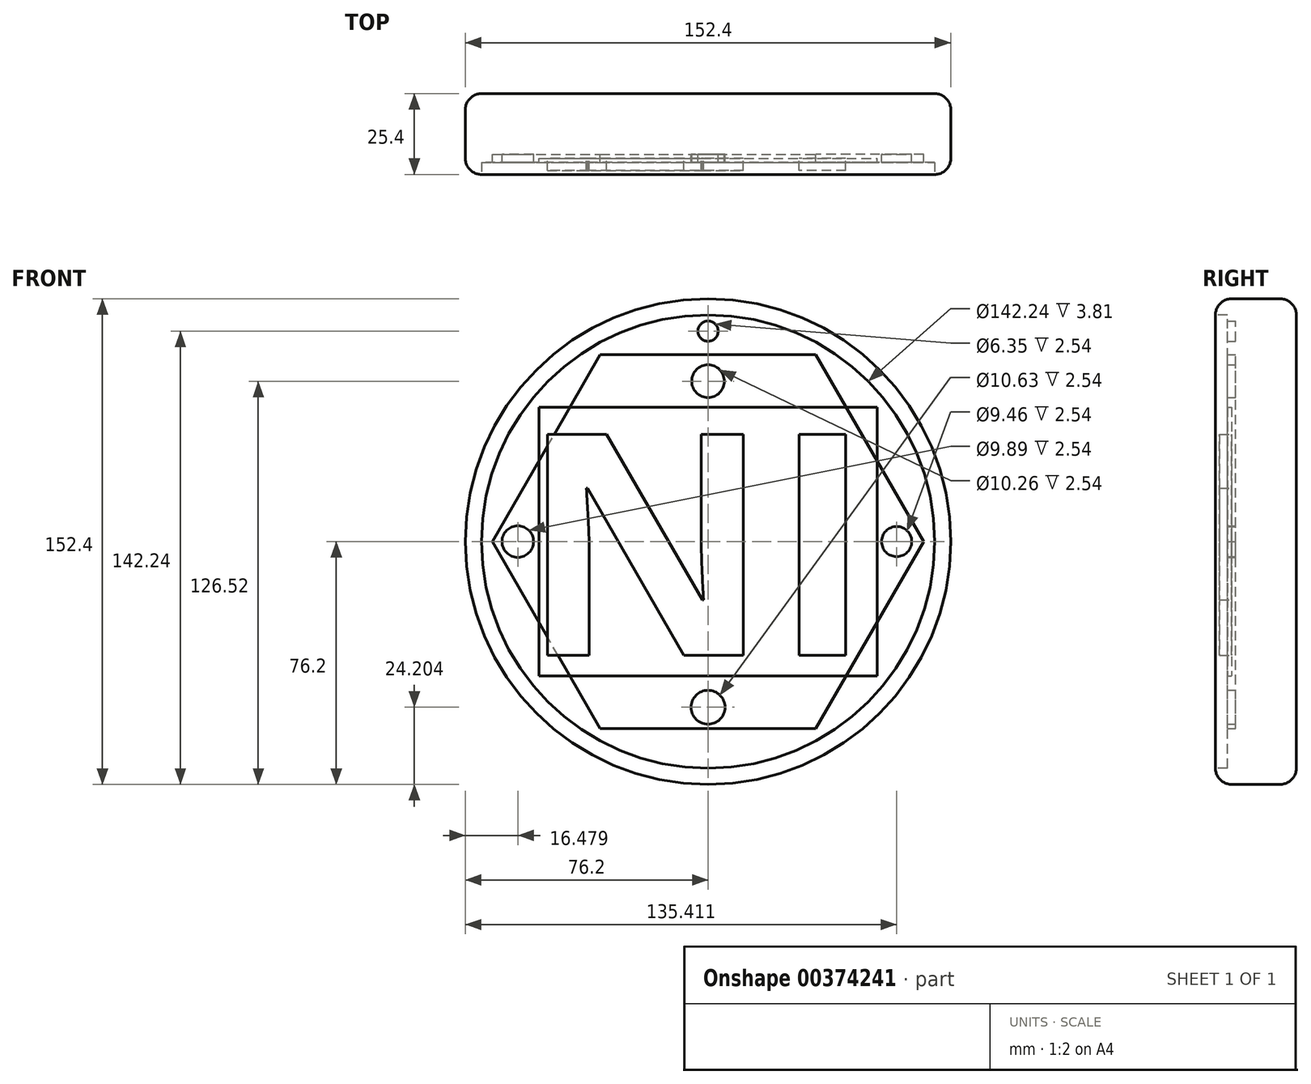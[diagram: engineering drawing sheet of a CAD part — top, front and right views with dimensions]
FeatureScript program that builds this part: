
annotation { "Feature Type Name" : "Feature", "Feature Type Description" : "" }
export const myFeature = defineFeature(function(context is Context, id is Id, definition is map)
    precondition{}
    {
        {
            var Q0;
            Q0=qCreatedBy(makeId("Front.planeOp"),FACE);
            var sketch = newSketch(context, id + "F0", { "sketchPlane" : qUnion([Q0])});
            skCircle(sketch, "E0", {"center": v(0, 0) * mm, "radius": 76.2 * mm});
            skSolve(sketch);
        }
        {
            var Q0;
            Q0=makeQuery(id+"F0.imprint","IMPRINT",FACE,{"disambiguationData":[TD([[makeQuery(id+"F0.imprint","IMPRINT",EDGE,{"derivedFrom":sQuery(id+"F0.wireOp",EDGE,"E0")}),1.0]])]});
            extrude(context, id + "F1", {"entities" : qUnion([Q0]), "depth" : 25.4 * mm});
        }
        {
            var Q0;
            Q0=makeQuery(id+"F1.opExtrude","CAP_EDGE",EDGE,{"disambiguationData":[OSD([sQuery(id+"F0.wireOp",EDGE,"E0")])],"isStart":false});
            var Q1;
            Q1=makeQuery(id+"F1.opExtrude","SWEPT_FACE",FACE,{"disambiguationData":[OSD([sQuery(id+"F0.wireOp",EDGE,"E0")])]});
            fillet(context, id + "F2", {"entities" : qUnion([Q0, Q1]), "radius" : 5.08 * mm, "tangentPropagation" : true, "allowEdgeOverflow" : false});
        }
        {
            var Q0;
            Q0=makeQuery(id+"F1.opExtrude","CAP_FACE",FACE,{"disambiguationData":[OSD([sQuery(id+"F0.wireOp",EDGE,"E0")])],"isStart":false});
            extrude(context, id + "F3", {"entities" : qUnion([Q0]), "operationType" : NewBodyOperationType.REMOVE, "oppositeDirection" : true, "depth" : 6.35 * mm});
        }
        {
            var Q0;
            Q0=makeQuery(id+"F3.boolean.opBoolean","COPY",FACE,{"derivedFrom":makeQuery(id+"F3.opExtrude","CAP_FACE",FACE,{"disambiguationData":[OSD([sQuery(id+"F0.wireOp",EDGE,"E0")])],"isStart":false})});
            var sketch = newSketch(context, id + "F4", { "sketchPlane" : qUnion([Q0])});
            skLineSegment(sketch, "E1", {"start": v(0, 0) * mm, "end": v(0, 66.04) * mm});
            skCircle(sketch, "E2", {"center": v(0, 66.04) * mm, "radius": 3.18 * mm});
            skSolve(sketch);
        }
        {
            var Q0;
            Q0=makeQuery(id+"F4.imprint","IMPRINT",FACE,{"disambiguationData":[TD([[makeQuery(id+"F4.imprint","IMPRINT",EDGE,{"derivedFrom":sQuery(id+"F4.wireOp",EDGE,"E2")}),-1.0]])]});
            var sketch = newSketch(context, id + "F5", { "sketchPlane" : qUnion([Q0])});
            skText(sketch, "E3", { "text": "NI", "fontName": "OpenSans-Bold.ttf"});
            const initialGuessF5  = {"E3": [-0.05916, -0.03572, 1, 0, 0.06994]};
            skSetInitialGuess(sketch, initialGuessF5);
            skSolve(sketch);
        }
        {
            var Q0;
            Q0=makeQuery(id+"F4.imprint","IMPRINT",FACE,{"disambiguationData":[TD([[makeQuery(id+"F4.imprint","IMPRINT",EDGE,{"derivedFrom":sQuery(id+"F4.wireOp",EDGE,"E2")}),-1.0]])]});
            var sketch = newSketch(context, id + "F6", { "sketchPlane" : qUnion([Q0])});
            skCircle(sketch, "E4.cCircle", {"center": v(0, 0) * mm, "radius": 58.64 * mm, "construction": true});
            skLineSegment(sketch, "E4.0", {"start": v(-33.85, 58.64) * mm, "end": v(33.85, 58.64) * mm});
            skLineSegment(sketch, "E4.1", {"start": v(33.85, 58.64) * mm, "end": v(67.7, 0) * mm});
            skLineSegment(sketch, "E4.2", {"start": v(67.7, 0) * mm, "end": v(33.85, -58.64) * mm});
            skLineSegment(sketch, "E4.3", {"start": v(33.85, -58.64) * mm, "end": v(-33.85, -58.64) * mm});
            skLineSegment(sketch, "E4.4", {"start": v(-33.85, -58.64) * mm, "end": v(-67.7, 0) * mm});
            skLineSegment(sketch, "E4.5", {"start": v(-67.7, 0) * mm, "end": v(-33.85, 58.64) * mm});
            skPoint(sketch, "E4.0.midPoint", {"position": v(0, 58.64) * mm});
            skSolve(sketch);
        }
        {
            var Q0;
            Q0=makeQuery(id+"F4.imprint","IMPRINT",FACE,{"disambiguationData":[TD([[makeQuery(id+"F4.imprint","IMPRINT",EDGE,{"derivedFrom":sQuery(id+"F4.wireOp",EDGE,"E2")}),-1.0]])]});
            var sketch = newSketch(context, id + "F7", { "sketchPlane" : qUnion([Q0])});
            skLineSegment(sketch, "E5.bottom", {"start": v(-53.05, 42.12) * mm, "end": v(53.05, 42.12) * mm});
            skLineSegment(sketch, "E5.top", {"start": v(-53.05, -42.12) * mm, "end": v(53.05, -42.12) * mm});
            skLineSegment(sketch, "E5.left", {"start": v(-53.05, 42.12) * mm, "end": v(-53.05, -42.12) * mm});
            skLineSegment(sketch, "E5.right", {"start": v(53.05, 42.12) * mm, "end": v(53.05, -42.12) * mm});
            skPoint(sketch, "E5.middle", {"position": v(0, 0) * mm});
            skSolve(sketch);
        }
        {
            var Q0;
            Q0 = qSketchRegion(id + "F5", true);
            extrude(context, id + "F8", {"entities" : qUnion([Q0]), "depth" : 5.08 * mm});
        }
        {
            var Q0;
            Q0=makeQuery(id+"F7.imprint","IMPRINT",FACE,{"disambiguationData":[TD([[makeQuery(id+"F7.imprint","IMPRINT",EDGE,{"derivedFrom":sQuery(id+"F7.wireOp",EDGE,"E5.bottom")}),1.0]])]});
            extrude(context, id + "F9", {"entities" : qUnion([Q0]), "operationType" : NewBodyOperationType.ADD, "depth" : 2.54 * mm});
        }
        {
            var Q0;
            Q0 = qSketchRegion(id + "F7", true);
            extrude(context, id + "F10", {"entities" : qUnion([Q0]), "operationType" : NewBodyOperationType.ADD, "depth" : 1.27 * mm});
        }
        {
            var Q0;
            Q0=makeQuery(id+"F4.imprint","IMPRINT",FACE,{"disambiguationData":[TD([[makeQuery(id+"F4.imprint","IMPRINT",EDGE,{"derivedFrom":sQuery(id+"F4.wireOp",EDGE,"E2")}),-1.0]])]});
            var sketch = newSketch(context, id + "F11", { "sketchPlane" : qUnion([Q0])});
            skCircle(sketch, "E6", {"center": v(0, 50.32) * mm, "radius": 5.13 * mm});
            skCircle(sketch, "E7", {"center": v(-59.72, 0) * mm, "radius": 4.95 * mm});
            skCircle(sketch, "E8", {"center": v(59.21, 0) * mm, "radius": 4.73 * mm});
            skCircle(sketch, "E9", {"center": v(0, -52) * mm, "radius": 5.32 * mm});
            skSolve(sketch);
        }
        {
            var Q0;
            Q0 = qSketchRegion(id + "F11", true);
            extrude(context, id + "F12", {"entities" : qUnion([Q0]), "operationType" : NewBodyOperationType.REMOVE, "depth" : 6.35 * mm});
        }
        {
            var Q0;
            Q0 = qSketchRegion(id + "F6", true);
            extrude(context, id + "F13", {"entities" : qUnion([Q0]), "depth" : 2.54 * mm});
        }
    });
